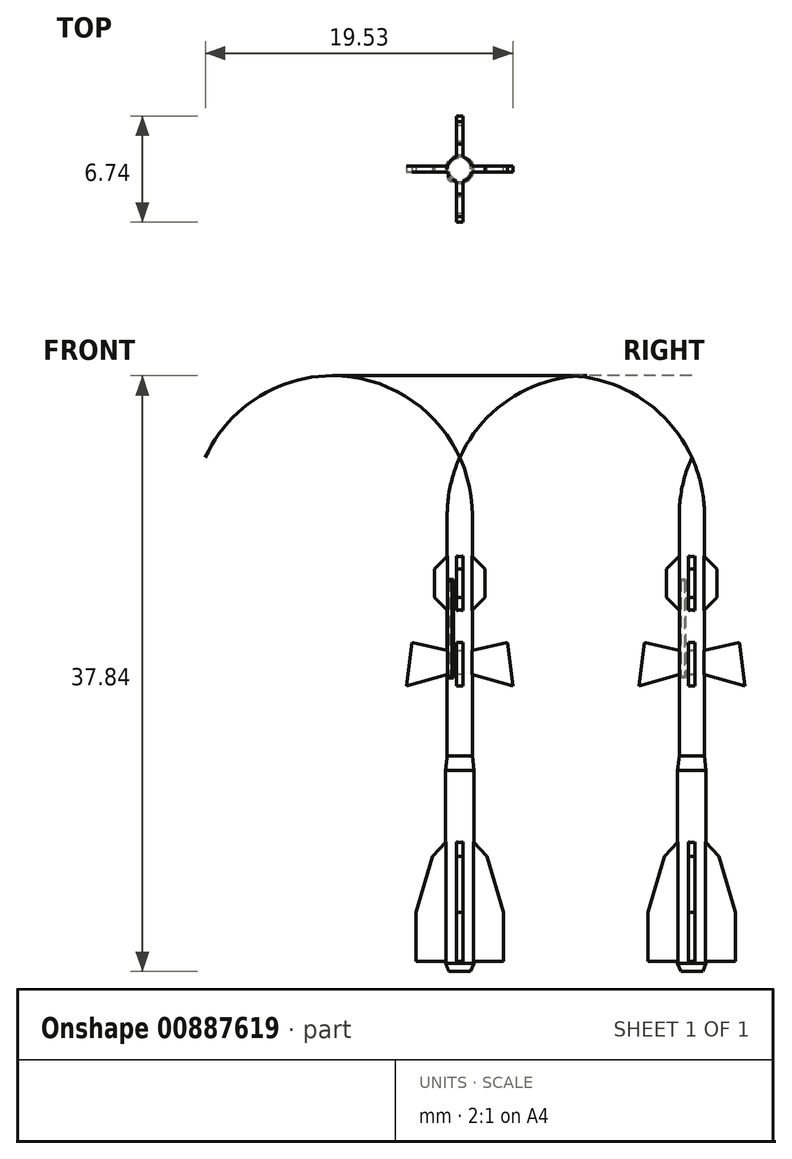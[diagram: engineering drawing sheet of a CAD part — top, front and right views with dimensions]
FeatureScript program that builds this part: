
annotation { "Feature Type Name" : "Feature", "Feature Type Description" : "" }
export const myFeature = defineFeature(function(context is Context, id is Id, definition is map)
    precondition{}
    {
        {
            assignVariable(context, id + "F0", {"name" : "s", "anyValue" : 144});
        }
        {
            var Q0;
            Q0=qCreatedBy(makeId("Front.planeOp"),FACE);
            var sketch = newSketch(context, id + "F1", { "sketchPlane" : qUnion([Q0])});
            skLineSegment(sketch, "E0", {"start": v(0, 0) * mm, "end": v(0, 32.64) * mm});
            skLineSegment(sketch, "E1", {"start": v(0.8, 28.96) * mm, "end": v(0.8, 0) * mm});
            skLineSegment(sketch, "E2", {"start": v(0.8, 0) * mm, "end": v(0, 0) * mm});
            skArc(sketch, "E3", {"start": v(0.8, 28.96) * mm, "mid": v(0.6, 30.84) * mm, "end": v(0, 32.64) * mm});
            skLineSegment(sketch, "E4", {"start": v(0.8, 13.68) * mm, "end": v(0.9, 12.78) * mm});
            skLineSegment(sketch, "E5", {"start": v(0.9, 12.78) * mm, "end": v(0.9, 0) * mm});
            skLineSegment(sketch, "E6", {"start": v(0.9, 0) * mm, "end": v(0.8, 0) * mm});
            skLineSegment(sketch, "E7", {"start": v(0.7, 0) * mm, "end": v(0.9, 0.52) * mm});
            skSolve(sketch);
        }
        {
            var Q0;
            {var subQ0=sQuery(id+"F1.wireOp",EDGE,"E4");Q0=makeQuery(id+"F1.imprint","IMPRINT",FACE,{"disambiguationData":[TD([[makeQuery(id+"F1.imprint","IMPRINT",EDGE,{"derivedFrom":subQ0}),-1.0]])]});}
            var Q1;
            {var subQ7=sQuery(id+"F1.wireOp",EDGE,"E0");Q1=makeQuery(id+"F1.imprint","IMPRINT",FACE,{"disambiguationData":[TD([[makeQuery(id+"F1.imprint","IMPRINT",EDGE,{"derivedFrom":subQ7}),-1.0]])]});}
            var Q2;
            Q2=sQuery(id+"F1.wireOp",EDGE,"E0");
            revolve(context, id + "F2", {"surfaceOperationType" : NewSurfaceOperationType.NEW, "entities" : qUnion([Q0, Q1]), "axis" : qUnion([Q2]), "revolveType" : RevolveType.FULL});
        }
        {
            var Q0;
            Q0=qCreatedBy(makeId("Front.planeOp"),FACE);
            var sketch = newSketch(context, id + "F3", { "sketchPlane" : qUnion([Q0])});
            skLineSegment(sketch, "E8", {"start": v(0, 0) * mm, "end": v(0, 27.15) * mm});
            skLineSegment(sketch, "E9", {"start": v(0, 27.15) * mm, "end": v(1.6, 25.56) * mm});
            skLineSegment(sketch, "E10", {"start": v(1.6, 25.56) * mm, "end": v(1.6, 23.75) * mm});
            skLineSegment(sketch, "E11", {"start": v(1.6, 23.75) * mm, "end": v(0.4, 22.55) * mm});
            skLineSegment(sketch, "E12", {"start": v(0.4, 22.55) * mm, "end": v(0.4, 20.3) * mm});
            skLineSegment(sketch, "E13", {"start": v(0.4, 20.3) * mm, "end": v(3.02, 20.9) * mm});
            skLineSegment(sketch, "E14", {"start": v(3.02, 20.9) * mm, "end": v(3.37, 18.12) * mm});
            skLineSegment(sketch, "E15", {"start": v(3.37, 18.13) * mm, "end": v(0.4, 18.96) * mm});
            skLineSegment(sketch, "E16", {"start": v(0.4, 18.96) * mm, "end": v(0.4, 8.74) * mm});
            skLineSegment(sketch, "E17", {"start": v(0.4, 8.74) * mm, "end": v(1.74, 7.3) * mm});
            skLineSegment(sketch, "E18", {"start": v(1.74, 7.3) * mm, "end": v(2.78, 3.75) * mm});
            skLineSegment(sketch, "E19", {"start": v(2.78, 3.75) * mm, "end": v(2.78, 0.63) * mm});
            skLineSegment(sketch, "E20", {"start": v(0.9, 0) * mm, "end": v(0.9, 32.87) * mm, "construction": true});
            skPoint(sketch, "E21", {"position": v(0.9, 8.2) * mm});
            skPoint(sketch, "E22", {"position": v(0.9, 18.82) * mm});
            skPoint(sketch, "E23", {"position": v(0.9, 20.42) * mm});
            skPoint(sketch, "E24", {"position": v(0.9, 23.06) * mm});
            skPoint(sketch, "E25", {"position": v(0.9, 26.25) * mm});
            skLineSegment(sketch, "E26", {"start": v(2.78, 0.63) * mm, "end": v(0, 0.63) * mm});
            skLineSegment(sketch, "E27.0", {"start": v(0.9, 0.52) * mm, "end": v(-0.9, 0.52) * mm});
            skSolve(sketch);
        }
        {
            var Q0;
            Q0=qSketchRegion(id+"F3",true);
            extrude(context, id + "F4", {"entities" : qUnion([Q0]), "operationType" : NewBodyOperationType.ADD, "depth" : .4 * mm, "offsetDistance" : 25 * mm, "symmetric" : true});
        }
        {
            var Q0;
            Q0=makeQuery(id+"F2.opRevolve","SWEPT_BODY",BODY,{"disambiguationData":[OSD([sQuery(id+"F1.wireOp",EDGE,"E0"),sQuery(id+"F1.wireOp",EDGE,"E1"),sQuery(id+"F1.wireOp",EDGE,"E2"),sQuery(id+"F1.wireOp",EDGE,"2EiOItwe-9FNA-eY8p-DkXH-AMy5AHyUmzZA"),sQuery(id+"F1.wireOp",EDGE,"E3")])]});
            var Q1;
            Q1=makeQuery(id+"F2.opRevolve","SWEPT_FACE",FACE,{"disambiguationData":[OSD([sQuery(id+"F1.wireOp",EDGE,"E1")])]});
            circularPattern(context, id + "F5", {"operationType" : NewBodyOperationType.ADD, "entities" : qUnion([Q0]), "axis" : qUnion([Q1]), "angle" : 360 * degree, "instanceCount" : 4, "equalSpace" : true, "computeTransformsWithoutBuiltin" : true});
        }
        {
            var Q0;
            Q0=qCreatedBy(makeId("Top.planeOp"),FACE);
            cPlane(context, id + "F6", {"entities" : qUnion([Q0]), "cplaneType" : CPlaneType.OFFSET, "offset" : (2700 / getVariable(context, 's')) * mm, "width" : 150 * mm, "height" : 150 * mm});
        }
        {
            var Q0;
            Q0=qCreatedBy(id+"F6.planeOp",FACE);
            var sketch = newSketch(context, id + "F7", { "sketchPlane" : qUnion([Q0])});
            skLineSegment(sketch, "E28", {"start": v(-0.08, -0.37) * mm, "end": v(-0.37, -0.08) * mm});
            skLineSegment(sketch, "E29", {"start": v(-0.37, -0.08) * mm, "end": v(-0.78, -0.48) * mm});
            skLineSegment(sketch, "E30", {"start": v(-0.48, -0.78) * mm, "end": v(-0.08, -0.37) * mm});
            skLineSegment(sketch, "E31", {"start": v(0, -0.64) * mm, "end": v(0, 0) * mm, "construction": true});
            skLineSegment(sketch, "E32", {"start": v(0, 0) * mm, "end": v(-0.22, -0.22) * mm, "construction": true});
            skArc(sketch, "E33", {"start": v(-0.78, -0.48) * mm, "mid": v(-0.7, -0.7) * mm, "end": v(-0.48, -0.78) * mm});
            skSolve(sketch);
        }
        {
            var Q0;
            Q0=qSketchRegion(id+"F7",true);
            extrude(context, id + "F8", {"entities" : qUnion([Q0]), "operationType" : NewBodyOperationType.ADD, "depth" : (870 / getVariable(context, 's')) * mm, "offsetDistance" : 25 * mm});
        }
        {
            var Q0;
            Q0=makeQuery(id+"F8.boolean.opBoolean","INTERSECT",EDGE,{"derivedFrom":[makeQuery(id+"F2.opRevolve","SWEPT_FACE",FACE,{"disambiguationData":[OSD([sQuery(id+"F1.wireOp",EDGE,"E1")])]}),makeQuery(id+"F8.opExtrude","CAP_FACE",FACE,{"disambiguationData":[OSD([sQuery(id+"F7.wireOp",EDGE,"E28"),sQuery(id+"F7.wireOp",EDGE,"E29"),sQuery(id+"F7.wireOp",EDGE,"E30"),sQuery(id+"F7.wireOp",EDGE,"E33")])],"isStart":false})]});
            var Q1;
            Q1=makeQuery(id+"F8.boolean.opBoolean","INTERSECT",EDGE,{"derivedFrom":[makeQuery(id+"F2.opRevolve","SWEPT_FACE",FACE,{"disambiguationData":[OSD([sQuery(id+"F1.wireOp",EDGE,"E1")])]}),makeQuery(id+"F8.opExtrude","CAP_FACE",FACE,{"disambiguationData":[OSD([sQuery(id+"F7.wireOp",EDGE,"E28"),sQuery(id+"F7.wireOp",EDGE,"E29"),sQuery(id+"F7.wireOp",EDGE,"E30"),sQuery(id+"F7.wireOp",EDGE,"E33")])],"isStart":true})]});
            chamfer(context, id + "F9", {"entities" : qUnion([Q0, Q1]), "width" : .1 * mm, "tangentPropagation" : true});
        }
    });
